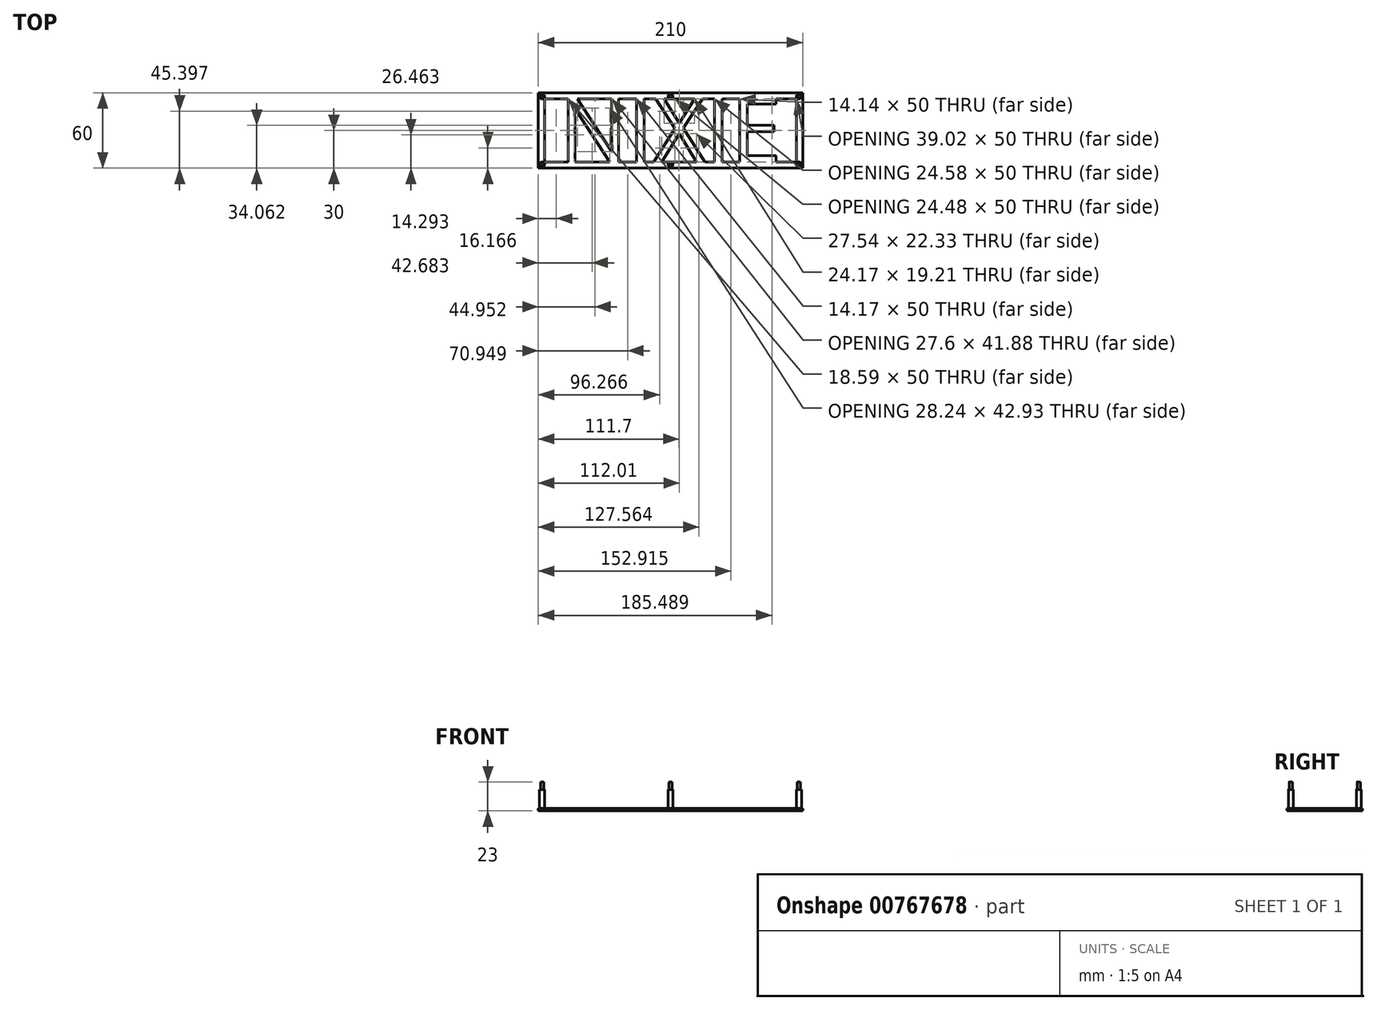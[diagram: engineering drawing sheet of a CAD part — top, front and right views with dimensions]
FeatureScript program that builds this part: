
annotation { "Feature Type Name" : "Feature", "Feature Type Description" : "" }
export const myFeature = defineFeature(function(context is Context, id is Id, definition is map)
    precondition{}
    {
        {
            var Q0;
            Q0=qCreatedBy(makeId("Top.planeOp"),FACE);
            var sketch = newSketch(context, id + "F0", { "sketchPlane" : qUnion([Q0])});
            skLineSegment(sketch, "E0.bottom", {"start": v(0, 0) * mm, "end": v(-210, 0) * mm});
            skLineSegment(sketch, "E0.top", {"start": v(0, 60) * mm, "end": v(-210, 60) * mm});
            skLineSegment(sketch, "E0.left", {"start": v(0, 0) * mm, "end": v(0, 60) * mm});
            skLineSegment(sketch, "E0.right", {"start": v(-210, 0) * mm, "end": v(-210, 60) * mm});
            skLineSegment(sketch, "E1.bottom", {"start": v(-5, 5) * mm, "end": v(-205, 5) * mm});
            skLineSegment(sketch, "E1.top", {"start": v(-5, 55) * mm, "end": v(-205, 55) * mm});
            skLineSegment(sketch, "E1.left", {"start": v(-5, 5) * mm, "end": v(-5, 55) * mm});
            skLineSegment(sketch, "E1.right", {"start": v(-205, 5) * mm, "end": v(-205, 55) * mm});
            skPoint(sketch, "E1.middle", {"position": v(-105, 30) * mm});
            skLineSegment(sketch, "E2", {"start": v(-105, 30) * mm, "end": v(-105, 60) * mm, "construction": true});
            skLineSegment(sketch, "E3", {"start": v(-105, 30) * mm, "end": v(0, 30) * mm, "construction": true});
            skLineSegment(sketch, "E4", {"start": v(-105, 5) * mm, "end": v(-105, 55) * mm, "construction": true});
            skSolve(sketch);
        }
        {
            var Q0;
            Q0 = qSketchRegion(id + "F0", true);
            extrude(context, id + "F1", {"entities" : qUnion([Q0]), "depth" : 2 * mm, "offsetDistance" : 25 * mm});
        }
        {
            var Q0;
            Q0=makeQuery(id+"F1.opExtrude","CAP_FACE",FACE,{"disambiguationData":[OSD([sQuery(id+"F0.wireOp",EDGE,"E0.bottom"),sQuery(id+"F0.wireOp",EDGE,"E0.top"),sQuery(id+"F0.wireOp",EDGE,"E0.left"),sQuery(id+"F0.wireOp",EDGE,"E0.right"),sQuery(id+"F0.wireOp",EDGE,"E1.bottom"),sQuery(id+"F0.wireOp",EDGE,"E1.top"),sQuery(id+"F0.wireOp",EDGE,"E1.left"),sQuery(id+"F0.wireOp",EDGE,"E1.right")])],"isStart":false});
            var sketch = newSketch(context, id + "F2", { "sketchPlane" : qUnion([Q0])});
            skCircle(sketch, "E5", {"center": v(-207, 3) * mm, "radius": 2 * mm});
            skLineSegment(sketch, "E6", {"start": v(-207, 3) * mm, "end": v(-210, 3) * mm, "construction": true});
            skLineSegment(sketch, "E7", {"start": v(-207, 3) * mm, "end": v(-207, 0) * mm, "construction": true});
            skCircle(sketch, "E8", {"center": v(-207, 57) * mm, "radius": 2 * mm});
            skCircle(sketch, "E9", {"center": v(-3, 57) * mm, "radius": 2 * mm});
            skLineSegment(sketch, "E10", {"start": v(-3, 57) * mm, "end": v(0, 57) * mm, "construction": true});
            skLineSegment(sketch, "E11", {"start": v(-3, 57) * mm, "end": v(-3, 60) * mm, "construction": true});
            skLineSegment(sketch, "E12", {"start": v(-207, 57) * mm, "end": v(-207, 60) * mm, "construction": true});
            skLineSegment(sketch, "E13", {"start": v(-207, 57) * mm, "end": v(-210, 57) * mm, "construction": true});
            skCircle(sketch, "E14", {"center": v(-3, 3) * mm, "radius": 2 * mm});
            skLineSegment(sketch, "E15", {"start": v(-3, 3) * mm, "end": v(0, 3) * mm, "construction": true});
            skLineSegment(sketch, "E16", {"start": v(-3, 3) * mm, "end": v(-3, 0) * mm, "construction": true});
            skCircle(sketch, "E17", {"center": v(-105, 3) * mm, "radius": 2 * mm});
            skPoint(sketch, "E17.centerSnap0", {"position": v(-105, 5) * mm});
            skCircle(sketch, "E18", {"center": v(-105, 57) * mm, "radius": 2 * mm});
            skPoint(sketch, "E18.centerSnap0", {"position": v(-105, 55) * mm});
            skSolve(sketch);
        }
        {
            var Q0;
            Q0 = qSketchRegion(id + "F2", true);
            var Q1;
            Q1 = qSketchRegion(id + "F4", true);
            extrude(context, id + "F3", {"entities" : qUnion([Q0, Q1]), "operationType" : NewBodyOperationType.ADD, "depth" : 15 * mm, "offsetDistance" : 25 * mm});
        }
        {
            var Q0;
            Q0=makeQuery(id+"F3.opExtrude","CAP_FACE",FACE,{"disambiguationData":[OSD([sQuery(id+"F2.wireOp",EDGE,"E5")])],"isStart":false});
            var sketch = newSketch(context, id + "F4", { "sketchPlane" : qUnion([Q0])});
            skCircle(sketch, "E19", {"center": v(-207, 3) * mm, "radius": 1.25 * mm});
            skSolve(sketch);
        }
        {
            var Q0;
            Q0=makeQuery(id+"F3.opExtrude","CAP_FACE",FACE,{"disambiguationData":[OSD([sQuery(id+"F2.wireOp",EDGE,"84402b22-fe5a-4893-9c25-d08e0c3cf2b3")])],"isStart":false});
            var Q1;
            Q1 = qSketchRegion(id + "F4", true);
            extrude(context, id + "F5", {"entities" : qUnion([Q0, Q1]), "operationType" : NewBodyOperationType.ADD, "depth" : 6 * mm, "offsetDistance" : 25 * mm});
        }
        {
            var Q0;
            Q0=makeQuery(id+"F3.opExtrude","CAP_FACE",FACE,{"disambiguationData":[OSD([sQuery(id+"F2.wireOp",EDGE,"E14")])],"isStart":false});
            var sketch = newSketch(context, id + "F6", { "sketchPlane" : qUnion([Q0])});
            skCircle(sketch, "E20", {"center": v(-3, 3) * mm, "radius": 1.25 * mm});
            skSolve(sketch);
        }
        {
            var Q0;
            Q0 = qSketchRegion(id + "F6", true);
            extrude(context, id + "F7", {"entities" : qUnion([Q0]), "operationType" : NewBodyOperationType.ADD, "depth" : 6 * mm, "offsetDistance" : 25 * mm});
        }
        {
            var Q0;
            Q0=makeQuery(id+"F3.opExtrude","CAP_FACE",FACE,{"disambiguationData":[OSD([sQuery(id+"F2.wireOp",EDGE,"E9")])],"isStart":false});
            var sketch = newSketch(context, id + "F8", { "sketchPlane" : qUnion([Q0])});
            skCircle(sketch, "E21", {"center": v(-3, 57) * mm, "radius": 1.25 * mm});
            skSolve(sketch);
        }
        {
            var Q0;
            Q0 = qSketchRegion(id + "F8", true);
            extrude(context, id + "F9", {"entities" : qUnion([Q0]), "operationType" : NewBodyOperationType.ADD, "depth" : 6 * mm, "offsetDistance" : 25 * mm});
        }
        {
            var Q0;
            Q0=makeQuery(id+"F3.opExtrude","CAP_FACE",FACE,{"disambiguationData":[OSD([sQuery(id+"F2.wireOp",EDGE,"E8")])],"isStart":false});
            var sketch = newSketch(context, id + "F10", { "sketchPlane" : qUnion([Q0])});
            skCircle(sketch, "E22", {"center": v(-207, 57) * mm, "radius": 1.25 * mm});
            skSolve(sketch);
        }
        {
            var Q0;
            Q0 = qSketchRegion(id + "F10", true);
            extrude(context, id + "F11", {"entities" : qUnion([Q0]), "operationType" : NewBodyOperationType.ADD, "depth" : 6 * mm, "offsetDistance" : 25 * mm});
        }
        {
            var Q0;
            Q0=qCreatedBy(makeId("Top.planeOp"),FACE);
            var sketch = newSketch(context, id + "F12", { "sketchPlane" : qUnion([Q0])});
            skText(sketch, "E23", { "text": "NIXIE", "fontName": "OpenSans-Regular.ttf"});
            const initialGuessF12  = {"E23": [-0.1935, 0.00466, 1, 0, 0.052]};
            skSetInitialGuess(sketch, initialGuessF12);
            skSolve(sketch);
        }
        {
            var Q0;
            Q0 = qSketchRegion(id + "F12", true);
            extrude(context, id + "F13", {"entities" : qUnion([Q0]), "operationType" : NewBodyOperationType.ADD, "depth" : 2 * mm, "offsetDistance" : 25 * mm});
        }
        {
            var Q0;
            Q0=makeQuery(id+"F3.opExtrude","CAP_FACE",FACE,{"disambiguationData":[OSD([sQuery(id+"F2.wireOp",EDGE,"E17")])],"isStart":false});
            var sketch = newSketch(context, id + "F14", { "sketchPlane" : qUnion([Q0])});
            skCircle(sketch, "E24", {"center": v(-105, 3) * mm, "radius": 1.25 * mm});
            skSolve(sketch);
        }
        {
            var Q0;
            Q0 = qSketchRegion(id + "F14", true);
            extrude(context, id + "F15", {"entities" : qUnion([Q0]), "operationType" : NewBodyOperationType.ADD, "depth" : 6 * mm, "offsetDistance" : 25 * mm});
        }
        {
            var Q0;
            Q0=makeQuery(id+"F3.opExtrude","CAP_FACE",FACE,{"disambiguationData":[OSD([sQuery(id+"F2.wireOp",EDGE,"E18")])],"isStart":false});
            var sketch = newSketch(context, id + "F16", { "sketchPlane" : qUnion([Q0])});
            skCircle(sketch, "E25", {"center": v(-105, 57) * mm, "radius": 1.25 * mm});
            skSolve(sketch);
        }
        {
            var Q0;
            Q0 = qSketchRegion(id + "F16", true);
            extrude(context, id + "F17", {"entities" : qUnion([Q0]), "operationType" : NewBodyOperationType.ADD, "depth" : 6 * mm, "offsetDistance" : 25 * mm});
        }
    });
